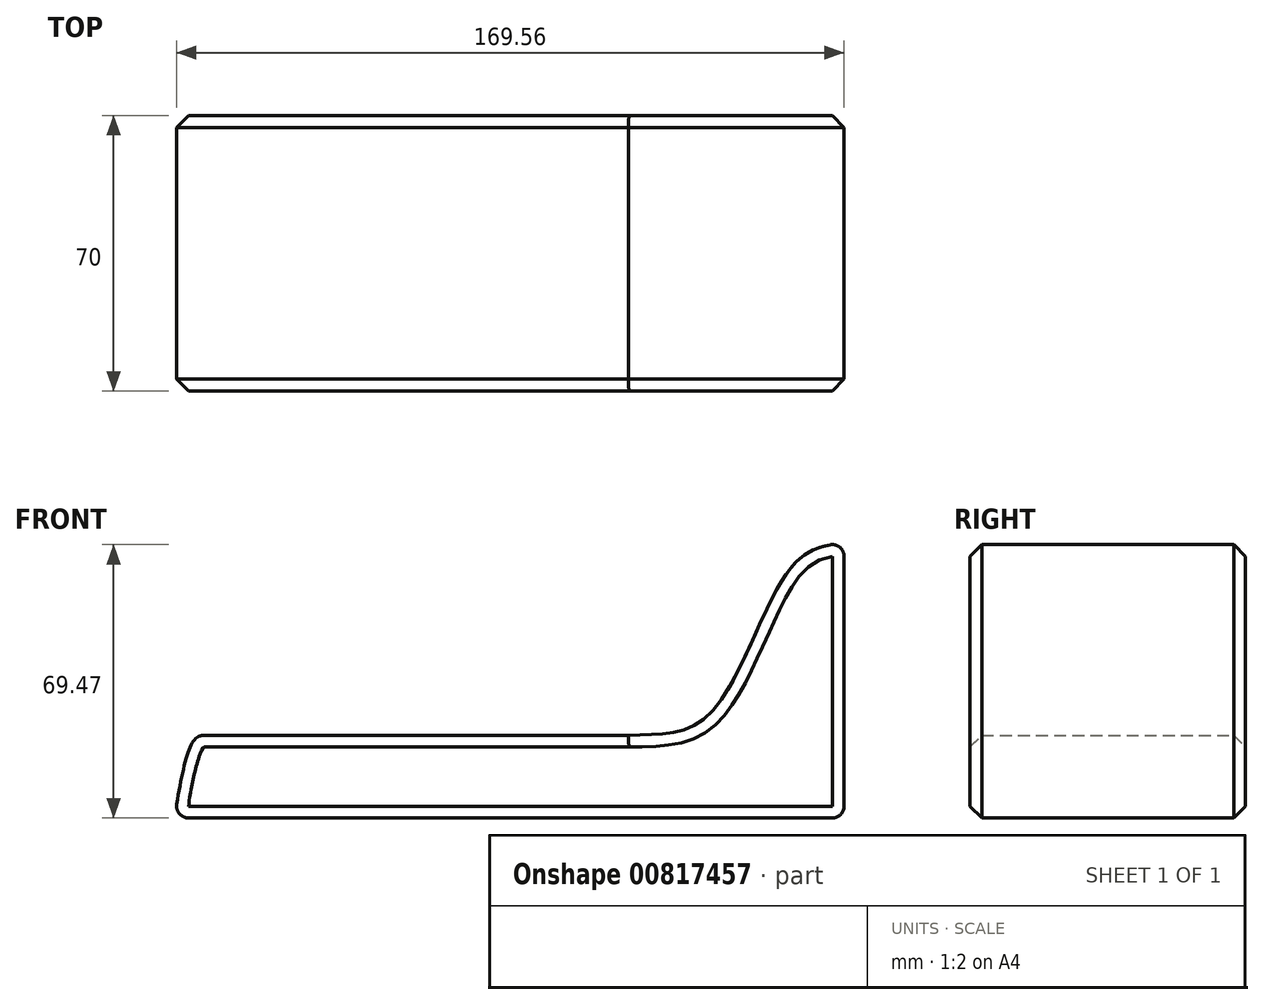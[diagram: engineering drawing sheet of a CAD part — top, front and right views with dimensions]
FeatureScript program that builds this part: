
annotation { "Feature Type Name" : "Feature", "Feature Type Description" : "" }
export const myFeature = defineFeature(function(context is Context, id is Id, definition is map)
    precondition{}
    {
        {
            var Q0;
            Q0=qCreatedBy(makeId("Front.planeOp"),FACE);
            var sketch = newSketch(context, id + "F0", { "sketchPlane" : qUnion([Q0])});
            skLineSegment(sketch, "E0.bottom", {"start": v(0, 0) * mm, "end": v(170, 0) * mm});
            skLineSegment(sketch, "E0.top", {"start": v(0, 70) * mm, "end": v(170, 70) * mm});
            skLineSegment(sketch, "E0.left", {"start": v(0, 0) * mm, "end": v(0, 70) * mm});
            skLineSegment(sketch, "E0.right", {"start": v(170, 0) * mm, "end": v(170, 70) * mm});
            skPoint(sketch, "E1", {"position": v(0, 21) * mm});
            skLineSegment(sketch, "E2", {"start": v(0, 21) * mm, "end": v(170, 21) * mm});
            skPoint(sketch, "E2.endSnap0", {"position": v(170, 35) * mm});
            skFitSpline(sketch, "E3", {"points": [v(115.24, 21) * mm, v(135.6, 26.17) * mm, v(156.59, 63.72) * mm, v(170, 70) * mm], "startDerivative": vector(72.43, 3.63) * mm, "endDerivative": vector(54.24, 7.8) * mm});
            skFitSpline(sketch, "E4", {"points": [v(0, 0) * mm, v(4.05, 18.36) * mm, v(7.04, 21) * mm, v(17.37, 16.8) * mm], "startDerivative": vector(6.52, 52.18) * mm, "endDerivative": vector(27.3, -33.27) * mm});
            skPoint(sketch, "E5.orphan", {"position": v(10, 21) * mm});
            skSolve(sketch);
        }
        {
            var Q0;
            {var subQ0=sQuery(id+"F0.wireOp",EDGE,"E3");Q0=makeQuery(id+"F0.imprint","IMPRINT",FACE,{"disambiguationData":[TD([[makeQuery(id+"F0.imprint","IMPRINT",EDGE,{"derivedFrom":subQ0}),-1.0]])]});}
            var Q1;
            {var subQ5=sQuery(id+"F0.wireOp",EDGE,"E0.bottom");Q1=makeQuery(id+"F0.imprint","IMPRINT",FACE,{"disambiguationData":[TD([[makeQuery(id+"F0.imprint","IMPRINT",EDGE,{"derivedFrom":subQ5}),1.0]])]});}
            extrude(context, id + "F1", {"entities" : qUnion([Q0, Q1]), "depth" : 70 * mm, "offsetDistance" : 25.4 * mm});
        }
        {
            var Q0;
            Q0=makeQuery(id+"F1.opExtrude","SWEPT_EDGE",EDGE,{"disambiguationData":[OSD([sQuery(id+"F0.wireOp",EDGE,"E0.top"),sQuery(id+"F0.wireOp",EDGE,"E0.right"),sQuery(id+"F0.wireOp",EDGE,"E3")])]});
            var Q1;
            Q1=makeQuery(id+"F1.opExtrude","SWEPT_EDGE",EDGE,{"disambiguationData":[OSD([sQuery(id+"F0.wireOp",EDGE,"E0.bottom"),sQuery(id+"F0.wireOp",EDGE,"E0.right")])]});
            var Q2;
            Q2=makeQuery(id+"F1.opExtrude","SWEPT_EDGE",EDGE,{"disambiguationData":[OSD([sQuery(id+"F0.wireOp",EDGE,"E0.bottom"),sQuery(id+"F0.wireOp",EDGE,"E0.left"),sQuery(id+"F0.wireOp",EDGE,"E4")])]});
            var Q3;
            Q3=makeQuery(id+"F1.opExtrude","SWEPT_EDGE",EDGE,{"disambiguationData":[OSD([sQuery(id+"F0.wireOp",EDGE,"E2"),sQuery(id+"F0.wireOp",EDGE,"E4")])]});
            fillet(context, id + "F2", {"entities" : qUnion([Q0, Q1, Q2, Q3]), "radius" : 3 * mm, "tangentPropagation" : true, "allowEdgeOverflow" : false});
        }
        {
            var Q0;
            {var subQ0=sQuery(id+"F0.wireOp",EDGE,"E4");var subQ1=sQuery(id+"F0.wireOp",EDGE,"E0.bottom");Q0=makeQuery(id+"F2.opFillet","BLEND_EDGE",EDGE,{"blendedFrom":[makeQuery(id+"F1.opExtrude","SWEPT_EDGE",EDGE,{"disambiguationData":[OSD([subQ1,sQuery(id+"F0.wireOp",EDGE,"E0.left"),subQ0])]}),makeQuery(id+"F1.opExtrude","CAP_FACE",FACE,{"disambiguationData":[OSD([subQ1,sQuery(id+"F0.wireOp",EDGE,"E0.right"),sQuery(id+"F0.wireOp",EDGE,"E2"),sQuery(id+"F0.wireOp",EDGE,"E3"),subQ0])],"isStart":true})],"blendedInto":[makeQuery(id+"F1.opExtrude","CAP_FACE",FACE,{"disambiguationData":[OSD([subQ1,sQuery(id+"F0.wireOp",EDGE,"E0.right"),sQuery(id+"F0.wireOp",EDGE,"E2"),sQuery(id+"F0.wireOp",EDGE,"E3"),subQ0])],"isStart":true})]});}
            var Q1;
            Q1=makeQuery(id+"F1.opExtrude","CAP_EDGE",EDGE,{"disambiguationData":[OSD([sQuery(id+"F0.wireOp",EDGE,"E4")])],"isStart":true});
            var Q2;
            {var subQ0=sQuery(id+"F0.wireOp",EDGE,"E4");var subQ1=sQuery(id+"F0.wireOp",EDGE,"E2");Q2=makeQuery(id+"F2.opFillet","BLEND_EDGE",EDGE,{"blendedFrom":[makeQuery(id+"F1.opExtrude","SWEPT_EDGE",EDGE,{"disambiguationData":[OSD([subQ1,subQ0])]}),makeQuery(id+"F1.opExtrude","CAP_FACE",FACE,{"disambiguationData":[OSD([sQuery(id+"F0.wireOp",EDGE,"E0.bottom"),sQuery(id+"F0.wireOp",EDGE,"E0.right"),subQ1,sQuery(id+"F0.wireOp",EDGE,"E3"),subQ0])],"isStart":true})],"blendedInto":[makeQuery(id+"F1.opExtrude","CAP_FACE",FACE,{"disambiguationData":[OSD([sQuery(id+"F0.wireOp",EDGE,"E0.bottom"),sQuery(id+"F0.wireOp",EDGE,"E0.right"),subQ1,sQuery(id+"F0.wireOp",EDGE,"E3"),subQ0])],"isStart":true})]});}
            var Q3;
            Q3=makeQuery(id+"F1.opExtrude","CAP_EDGE",EDGE,{"disambiguationData":[OSD([sQuery(id+"F0.wireOp",EDGE,"E2")])],"isStart":true});
            var Q4;
            Q4=makeQuery(id+"F1.opExtrude","CAP_EDGE",EDGE,{"disambiguationData":[OSD([sQuery(id+"F0.wireOp",EDGE,"E0.bottom")])],"isStart":true});
            var Q5;
            {var subQ0=sQuery(id+"F0.wireOp",EDGE,"E4");var subQ1=sQuery(id+"F0.wireOp",EDGE,"E0.bottom");Q5=makeQuery(id+"F2.opFillet","BLEND_EDGE",EDGE,{"blendedFrom":[makeQuery(id+"F1.opExtrude","SWEPT_EDGE",EDGE,{"disambiguationData":[OSD([subQ1,sQuery(id+"F0.wireOp",EDGE,"E0.left"),subQ0])]}),makeQuery(id+"F1.opExtrude","CAP_FACE",FACE,{"disambiguationData":[OSD([subQ1,sQuery(id+"F0.wireOp",EDGE,"E0.right"),sQuery(id+"F0.wireOp",EDGE,"E2"),sQuery(id+"F0.wireOp",EDGE,"E3"),subQ0])],"isStart":false})],"blendedInto":[makeQuery(id+"F1.opExtrude","CAP_FACE",FACE,{"disambiguationData":[OSD([subQ1,sQuery(id+"F0.wireOp",EDGE,"E0.right"),sQuery(id+"F0.wireOp",EDGE,"E2"),sQuery(id+"F0.wireOp",EDGE,"E3"),subQ0])],"isStart":false})]});}
            var Q6;
            Q6=makeQuery(id+"F1.opExtrude","CAP_EDGE",EDGE,{"disambiguationData":[OSD([sQuery(id+"F0.wireOp",EDGE,"E0.bottom")])],"isStart":false});
            var Q7;
            Q7=makeQuery(id+"F1.opExtrude","CAP_EDGE",EDGE,{"disambiguationData":[OSD([sQuery(id+"F0.wireOp",EDGE,"E4")])],"isStart":false});
            var Q8;
            {var subQ0=sQuery(id+"F0.wireOp",EDGE,"E4");var subQ1=sQuery(id+"F0.wireOp",EDGE,"E2");Q8=makeQuery(id+"F2.opFillet","BLEND_EDGE",EDGE,{"blendedFrom":[makeQuery(id+"F1.opExtrude","SWEPT_EDGE",EDGE,{"disambiguationData":[OSD([subQ1,subQ0])]}),makeQuery(id+"F1.opExtrude","CAP_FACE",FACE,{"disambiguationData":[OSD([sQuery(id+"F0.wireOp",EDGE,"E0.bottom"),sQuery(id+"F0.wireOp",EDGE,"E0.right"),subQ1,sQuery(id+"F0.wireOp",EDGE,"E3"),subQ0])],"isStart":false})],"blendedInto":[makeQuery(id+"F1.opExtrude","CAP_FACE",FACE,{"disambiguationData":[OSD([sQuery(id+"F0.wireOp",EDGE,"E0.bottom"),sQuery(id+"F0.wireOp",EDGE,"E0.right"),subQ1,sQuery(id+"F0.wireOp",EDGE,"E3"),subQ0])],"isStart":false})]});}
            var Q9;
            Q9=makeQuery(id+"F1.opExtrude","CAP_EDGE",EDGE,{"disambiguationData":[OSD([sQuery(id+"F0.wireOp",EDGE,"E2")])],"isStart":false});
            var Q10;
            {var subQ0=sQuery(id+"F0.wireOp",EDGE,"E0.right");var subQ1=sQuery(id+"F0.wireOp",EDGE,"E0.bottom");Q10=makeQuery(id+"F2.opFillet","BLEND_EDGE",EDGE,{"blendedFrom":[makeQuery(id+"F1.opExtrude","SWEPT_EDGE",EDGE,{"disambiguationData":[OSD([subQ1,subQ0])]}),makeQuery(id+"F1.opExtrude","CAP_FACE",FACE,{"disambiguationData":[OSD([subQ1,subQ0,sQuery(id+"F0.wireOp",EDGE,"E2"),sQuery(id+"F0.wireOp",EDGE,"E3"),sQuery(id+"F0.wireOp",EDGE,"E4")])],"isStart":true})],"blendedInto":[makeQuery(id+"F1.opExtrude","CAP_FACE",FACE,{"disambiguationData":[OSD([subQ1,subQ0,sQuery(id+"F0.wireOp",EDGE,"E2"),sQuery(id+"F0.wireOp",EDGE,"E3"),sQuery(id+"F0.wireOp",EDGE,"E4")])],"isStart":true})]});}
            var Q11;
            {var subQ0=sQuery(id+"F0.wireOp",EDGE,"E0.right");var subQ1=sQuery(id+"F0.wireOp",EDGE,"E0.bottom");Q11=makeQuery(id+"F2.opFillet","BLEND_EDGE",EDGE,{"blendedFrom":[makeQuery(id+"F1.opExtrude","SWEPT_EDGE",EDGE,{"disambiguationData":[OSD([subQ1,subQ0])]}),makeQuery(id+"F1.opExtrude","CAP_FACE",FACE,{"disambiguationData":[OSD([subQ1,subQ0,sQuery(id+"F0.wireOp",EDGE,"E2"),sQuery(id+"F0.wireOp",EDGE,"E3"),sQuery(id+"F0.wireOp",EDGE,"E4")])],"isStart":false})],"blendedInto":[makeQuery(id+"F1.opExtrude","CAP_FACE",FACE,{"disambiguationData":[OSD([subQ1,subQ0,sQuery(id+"F0.wireOp",EDGE,"E2"),sQuery(id+"F0.wireOp",EDGE,"E3"),sQuery(id+"F0.wireOp",EDGE,"E4")])],"isStart":false})]});}
            var Q12;
            Q12=makeQuery(id+"F1.opExtrude","CAP_EDGE",EDGE,{"disambiguationData":[OSD([sQuery(id+"F0.wireOp",EDGE,"E0.right")])],"isStart":false});
            var Q13;
            Q13=makeQuery(id+"F1.opExtrude","CAP_EDGE",EDGE,{"disambiguationData":[OSD([sQuery(id+"F0.wireOp",EDGE,"E3")])],"isStart":false});
            var Q14;
            {var subQ0=sQuery(id+"F0.wireOp",EDGE,"E3");var subQ1=sQuery(id+"F0.wireOp",EDGE,"E0.right");Q14=makeQuery(id+"F2.opFillet","BLEND_EDGE",EDGE,{"blendedFrom":[makeQuery(id+"F1.opExtrude","SWEPT_EDGE",EDGE,{"disambiguationData":[OSD([sQuery(id+"F0.wireOp",EDGE,"E0.top"),subQ1,subQ0])]}),makeQuery(id+"F1.opExtrude","CAP_FACE",FACE,{"disambiguationData":[OSD([sQuery(id+"F0.wireOp",EDGE,"E0.bottom"),subQ1,sQuery(id+"F0.wireOp",EDGE,"E2"),subQ0,sQuery(id+"F0.wireOp",EDGE,"E4")])],"isStart":false})],"blendedInto":[makeQuery(id+"F1.opExtrude","CAP_FACE",FACE,{"disambiguationData":[OSD([sQuery(id+"F0.wireOp",EDGE,"E0.bottom"),subQ1,sQuery(id+"F0.wireOp",EDGE,"E2"),subQ0,sQuery(id+"F0.wireOp",EDGE,"E4")])],"isStart":false})]});}
            var Q15;
            Q15=makeQuery(id+"F1.opExtrude","CAP_EDGE",EDGE,{"disambiguationData":[OSD([sQuery(id+"F0.wireOp",EDGE,"E0.right")])],"isStart":true});
            var Q16;
            {var subQ0=sQuery(id+"F0.wireOp",EDGE,"E3");var subQ1=sQuery(id+"F0.wireOp",EDGE,"E0.right");Q16=makeQuery(id+"F2.opFillet","BLEND_EDGE",EDGE,{"blendedFrom":[makeQuery(id+"F1.opExtrude","SWEPT_EDGE",EDGE,{"disambiguationData":[OSD([sQuery(id+"F0.wireOp",EDGE,"E0.top"),subQ1,subQ0])]}),makeQuery(id+"F1.opExtrude","CAP_FACE",FACE,{"disambiguationData":[OSD([sQuery(id+"F0.wireOp",EDGE,"E0.bottom"),subQ1,sQuery(id+"F0.wireOp",EDGE,"E2"),subQ0,sQuery(id+"F0.wireOp",EDGE,"E4")])],"isStart":true})],"blendedInto":[makeQuery(id+"F1.opExtrude","CAP_FACE",FACE,{"disambiguationData":[OSD([sQuery(id+"F0.wireOp",EDGE,"E0.bottom"),subQ1,sQuery(id+"F0.wireOp",EDGE,"E2"),subQ0,sQuery(id+"F0.wireOp",EDGE,"E4")])],"isStart":true})]});}
            var Q17;
            Q17=makeQuery(id+"F1.opExtrude","CAP_EDGE",EDGE,{"disambiguationData":[OSD([sQuery(id+"F0.wireOp",EDGE,"E3")])],"isStart":true});
            chamfer(context, id + "F3", {"entities" : qUnion([Q0, Q1, Q2, Q3, Q4, Q5, Q6, Q7, Q8, Q9, Q10, Q11, Q12, Q13, Q14, Q15, Q16, Q17]), "width" : 3 * mm, "tangentPropagation" : true});
        }
    });
